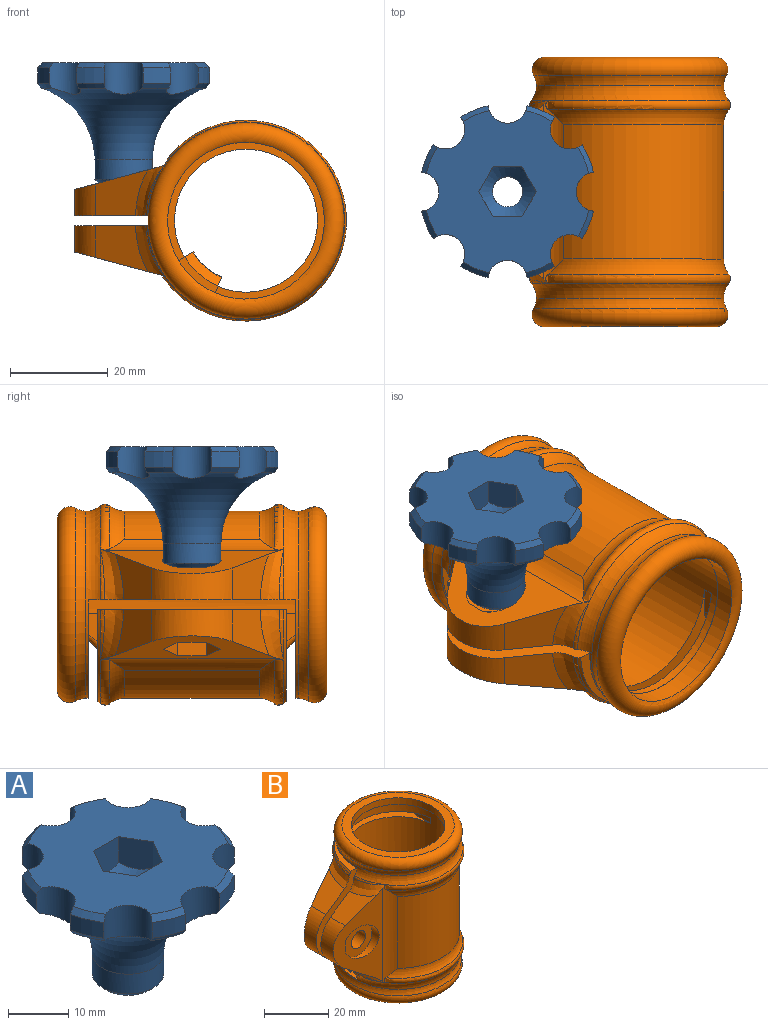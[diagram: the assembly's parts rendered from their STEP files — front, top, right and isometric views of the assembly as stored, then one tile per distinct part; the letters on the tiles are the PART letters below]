
ASSEMBLY  parts=2 mates=1
PART A: 45 faces, bbox 45.5x45.5x30.6 mm
  f0: plane 33.17x33.17mm, normal (0,0,1), area 688.8mm2, adj f2,f5,f8,f11,f14,f17,f21,f27
  f1: cone r=18mm half-angle=37.9deg, axis (0,0,1), area 7.3mm2, adj f23,f24,f36,f43
  f2: cone r=17mm half-angle=45deg, axis (0,0,-1), area 8.4mm2, adj f0,f24,f36,f43
  f3: cylinder r=18mm len=5.63mm, axis (0,0,1), area 19.6mm2, adj f4,f5,f42,f43
  f4: cone r=18mm half-angle=37.9deg, axis (0,0,1), area 7.3mm2, adj f3,f23,f42,f43
  f5: cone r=17mm half-angle=45deg, axis (0,0,-1), area 8.4mm2, adj f0,f3,f42,f43
  f6: cylinder r=18mm len=5.63mm, axis (0,0,1), area 19.6mm2, adj f7,f8,f41,f42
  f7: cone r=18mm half-angle=37.9deg, axis (0,0,1), area 7.3mm2, adj f6,f23,f41,f42
  f8: cone r=17mm half-angle=45deg, axis (0,0,-1), area 8.4mm2, adj f0,f6,f41,f42
  f9: cylinder r=18mm len=5.63mm, axis (0,0,1), area 19.6mm2, adj f10,f11,f40,f41
  f10: cone r=18mm half-angle=37.9deg, axis (0,0,1), area 7.3mm2, adj f9,f23,f40,f41
  f11: cone r=17mm half-angle=45deg, axis (0,0,-1), area 8.4mm2, adj f0,f9,f40,f41
  f12: cylinder r=18mm len=5.63mm, axis (0,0,1), area 19.6mm2, adj f13,f14,f39,f40
  f13: cone r=18mm half-angle=37.9deg, axis (0,0,1), area 7.3mm2, adj f12,f23,f39,f40
  f14: cone r=17mm half-angle=45deg, axis (0,0,-1), area 8.4mm2, adj f0,f12,f39,f40
  f15: cylinder r=18mm len=5.63mm, axis (0,0,1), area 19.6mm2, adj f16,f17,f38,f39
  f16: cone r=18mm half-angle=37.9deg, axis (0,0,1), area 7.3mm2, adj f15,f23,f38,f39
  f17: cone r=17mm half-angle=45deg, axis (0,0,-1), area 8.4mm2, adj f0,f15,f38,f39
  f18: cylinder r=18mm len=5.63mm, axis (0,0,1), area 19.6mm2, adj f20,f21,f37,f38
  f19: cylinder r=18mm len=5.63mm, axis (0,0,1), area 19.6mm2, adj f34,f35,f36,f37
  f20: cone r=18mm half-angle=37.9deg, axis (0,0,1), area 7.3mm2, adj f18,f23,f37,f38
  f21: cone r=17mm half-angle=45deg, axis (0,0,-1), area 8.4mm2, adj f0,f18,f37,f38
  f22: cylinder r=3.1mm len=16.72mm, axis (0,0,1), area 325.6mm2, adj f25,f44
  f23: torus R=20.9mm, axis (0,0,1), area 1085.1mm2, adj f1,f4,f7,f10,f13,f16,f20,f26
  f24: cylinder r=18mm len=5.63mm, axis (0,0,1), area 19.6mm2, adj f1,f2,f36,f43
  f25: plane 9.8x9.8mm, normal (0,0,-1), area 45.2mm2, adj f22,f33
  f26: cylinder r=5.9mm len=11.8mm, axis (0,0,1), area 148.3mm2, adj f23,f33
  f27: plane 6.01x5.1mm, normal (0.87,-0.5,0), area 33.7mm2, adj f0,f28,f32,f44
  f28: plane 6.01x5.1mm, normal (0.87,0.5,0), area 33.7mm2, adj f0,f27,f29,f44
  f29: plane 6.01x5.89mm, normal (0,1,0), area 33.7mm2, adj f0,f28,f30,f44
  f30: plane 6.29x5.38mm, normal (-0.87,0.5,0), area 33.7mm2, adj f0,f29,f31,f44
  f31: plane 6.01x5.1mm, normal (-0.87,-0.5,0), area 33.7mm2, adj f0,f30,f32,f44
  f32: plane 6.01x5.89mm, normal (0,-1,0), area 33.7mm2, adj f0,f27,f31,f44
  f33: cone r=5.9mm half-angle=45deg, axis (0,0,1), area 48mm2, adj f25,f26
  f34: cone r=18mm half-angle=37.9deg, axis (0,0,1), area 7.3mm2, adj f19,f23,f36,f37
  f35: cone r=17mm half-angle=45deg, axis (0,0,-1), area 8.4mm2, adj f0,f19,f36,f37
  f36: cylinder r=4mm len=7.95mm, axis (0,0,1), area 65.9mm2, adj f0,f1,f2,f19,f23,f24,f34,f35
  f37: cylinder r=4mm len=6.5mm, axis (0,0,1), area 65.9mm2, adj f0,f18,f19,f20,f21,f23,f34,f35
  f38: cylinder r=4mm len=7.95mm, axis (0,0,1), area 65.9mm2, adj f0,f15,f16,f17,f18,f20,f21,f23
  f39: cylinder r=4mm len=6.5mm, axis (0,0,1), area 65.9mm2, adj f0,f12,f13,f14,f15,f16,f17,f23
  f40: cylinder r=4mm len=7.95mm, axis (0,0,1), area 64.9mm2, adj f0,f9,f10,f11,f12,f13,f14,f23
  f41: cylinder r=4mm len=6.5mm, axis (0,0,1), area 65.9mm2, adj f0,f6,f7,f8,f9,f10,f11,f23
  f42: cylinder r=4mm len=7.95mm, axis (0,0,1), area 65.9mm2, adj f0,f3,f4,f5,f6,f7,f8,f23
  f43: cylinder r=4mm len=6.5mm, axis (0,0,1), area 65.9mm2, adj f0,f1,f2,f3,f4,f5,f23,f24
  f44: cone r=3.1mm half-angle=45deg, axis (0,0,1), area 84.9mm2, adj f22,f27,f28,f29,f30,f31,f32
PART B: 99 faces, bbox 63.5x50.8x61.3 mm
  f0: cylinder r=12.5mm len=5.83mm, axis (0,0,1), area 2.4mm2, adj f1,f96,f97,f98
  f1: cone r=12.5mm half-angle=45deg, axis (0,0,-1), area 6.9mm2, adj f0,f2,f96,f98
  f2: cone r=13.1mm half-angle=45deg, axis (0,0,1), area 5.7mm2, adj f1,f3,f96,f98
  f3: cone r=12.5mm half-angle=45deg, axis (0,0,-1), area 23mm2, adj f2,f4,f96,f98
  f4: plane 8.14x7.42mm, normal (0,0,-1), area 15.5mm2, adj f3,f5,f96,f98
  f5: cylinder r=16.1mm len=47.93mm, axis (0,0,-1), area 4368.8mm2, adj f4,f6,f58,f59,f60,f61,f62,f63
  f6: plane 38.5x18.97mm, normal (0,-1,0), area 431.9mm2, adj f5,f7,f38,f39,f40,f41,f42,f49
  f7: cylinder r=3.1mm len=6.51mm, axis (0,-1,0), area 126.8mm2, adj f6,f8
  f8: plane 11.78x10.2mm, normal (0,1,0), area 59.9mm2, adj f7,f9,f33,f34,f35,f36,f37
  f9: plane 5.1x2.94mm, normal (0.5,0,-0.87), area 5.1mm2, adj f8,f10,f33,f37
  f10: plane 37.81x19.56mm, normal (-0.26,0.97,0), area 303mm2, adj f9,f11,f33,f34,f35,f36,f37,f38
  f11: cylinder r=9mm len=36.95mm, axis (0,0,-1), area 151.5mm2, adj f10,f12,f27,f28,f29,f31,f40,f56
  f12: torus R=24.1mm, axis (0,0,-1), area 319.6mm2, adj f11,f13,f27,f31
  f13: cylinder r=9mm len=36.95mm, axis (0,0,-1), area 151.5mm2, adj f12,f14,f20,f24,f27,f28,f29,f31
  f14: bspline ~13.12x6.42mm, area 42.7mm2, adj f13,f15,f18,f19,f20,f42,f62
  f15: plane 10.75x9.41mm, normal (-0.58,0,0.82), area 84.9mm2, adj f14,f16,f20,f62
  f16: cylinder r=10mm len=16.34mm, axis (0,1,0), area 124.5mm2, adj f15,f17,f20,f62
  f17: plane 10.75x9.4mm, normal (-0.58,0,-0.82), area 84.9mm2, adj f16,f20,f24,f62
  f18: cylinder r=9mm len=0.26mm, axis (0,0,-1), area 0mm2, adj f14,f31,f42
  f19: torus R=19mm, axis (0,0,1), area 5mm2, adj f14,f42,f62
  f20: plane 41.85x23.6mm, normal (-0.26,-0.97,0), area 279.7mm2, adj f13,f14,f15,f16,f17,f21,f23,f24
  f21: plane 12x11.77mm, normal (0,-1,0), area 82.4mm2, adj f20,f22,f23
  f22: cylinder r=3.1mm len=6.51mm, axis (0,1,0), area 126.8mm2, adj f21,f62
  f23: cylinder r=6mm len=12mm, axis (0,-1,0), area 0mm2, adj f20,f21
  f24: bspline ~14.6x6.42mm, area 42.7mm2, adj f13,f17,f20,f25,f26,f49,f62
  f25: torus R=19mm, axis (0,0,1), area 5mm2, adj f24,f49,f62
  f26: cylinder r=9mm len=0.26mm, axis (0,0,-1), area 0mm2, adj f24,f29,f49
  f27: cylinder r=19.1mm len=38.2mm, axis (0,0,-1), area 2475.2mm2, adj f11,f12,f13,f28
  f28: torus R=24.1mm, axis (0,0,-1), area 319.6mm2, adj f11,f13,f27,f29
  f29: torus R=19mm, axis (0,0,1), area 209.4mm2, adj f11,f13,f26,f28,f30,f49
  f30: cylinder r=9mm len=0.26mm, axis (0,0,-1), area 0mm2, adj f29,f49,f56
  f31: torus R=19mm, axis (0,0,1), area 209.4mm2, adj f11,f12,f13,f18,f32,f42
  f32: cylinder r=9mm len=0.26mm, axis (0,0,-1), area 0mm2, adj f31,f40,f42
  f33: plane 5.89x0.18mm, normal (1,0,0), area 1mm2, adj f8,f9,f10,f34
  f34: plane 5.1x2.94mm, normal (0.5,0,0.87), area 5.1mm2, adj f8,f10,f33,f35
  f35: plane 5.1x2.94mm, normal (-0.5,0,0.87), area 13.1mm2, adj f8,f10,f34,f36
  f36: plane 5.89x2.91mm, normal (-1,0,0), area 17.1mm2, adj f8,f10,f35,f37
  f37: plane 5.1x2.94mm, normal (-0.5,0,-0.87), area 13.1mm2, adj f8,f9,f10,f36
  f38: cylinder r=10mm len=16.34mm, axis (0,-1,0), area 124.5mm2, adj f6,f10,f39,f57
  f39: plane 10.75x9.4mm, normal (-0.58,0,0.82), area 84.9mm2, adj f6,f10,f38,f40
  f40: bspline ~14.6x6.42mm, area 42.7mm2, adj f6,f10,f11,f32,f39,f41,f42
  f41: torus R=19mm, axis (0,0,1), area 5mm2, adj f6,f40,f42
  f42: torus R=24.1mm, axis (0,0,1), area 292.5mm2, adj f6,f14,f18,f19,f31,f32,f40,f41
  f43: torus R=24.09mm, axis (0,0,1), area 260.7mm2, adj f42,f44
  f44: torus R=17.5mm, axis (0,0,1), area 626.8mm2, adj f43,f45
  f45: plane 35x35mm, normal (0,0,1), area 292.5mm2, adj f44,f46
  f46: cylinder r=14.6mm len=29.2mm, axis (0,0,1), area 229.3mm2, adj f45,f63
  f47: bspline ~5.64x4.41mm, area 6.3mm2, adj f42,f48,f64,f66
  f48: plane 5.85x2mm, normal (-1,0,0), area 10mm2, adj f47,f64,f65,f66
  f49: torus R=24.1mm, axis (0,0,1), area 292.5mm2, adj f6,f24,f25,f26,f29,f30,f50,f52
  f50: bspline ~5.64x4.36mm, area 6.3mm2, adj f49,f51,f58,f61
  f51: plane 5.85x2mm, normal (-1,0,0), area 10mm2, adj f50,f58,f59,f61
  f52: torus R=24.09mm, axis (0,0,1), area 260.7mm2, adj f49,f53
  f53: torus R=17.5mm, axis (0,0,1), area 795.8mm2, adj f52,f54
  f54: cylinder r=16mm len=32mm, axis (0,0,1), area 402.1mm2, adj f53,f60
  f55: torus R=19mm, axis (0,0,1), area 5mm2, adj f6,f49,f56
  f56: bspline ~13.12x6.42mm, area 42.7mm2, adj f6,f10,f11,f30,f49,f55,f57
  f57: plane 10.75x9.41mm, normal (-0.58,0,-0.82), area 84.9mm2, adj f6,f10,f38,f56
  f58: plane 39.1x20.35mm, normal (0,0,-1), area 176.5mm2, adj f5,f6,f49,f50,f51,f59
  f59: cylinder r=1mm len=2mm, axis (0,0,-1), area 0.2mm2, adj f5,f51,f58,f61
  f60: torus R=17.5mm, axis (0,0,1), area 12.4mm2, adj f5,f54
  f61: plane 37.52x20.59mm, normal (0,0,1), area 151.6mm2, adj f5,f49,f50,f51,f59,f62
  f62: plane 42.51x18.97mm, normal (0,1,0), area 445mm2, adj f5,f14,f15,f16,f17,f19,f22,f24
  f63: plane 32.2x32.2mm, normal (0,0,-1), area 144.7mm2, adj f5,f46
  f64: plane 37.52x20.59mm, normal (0,0,-1), area 151.6mm2, adj f5,f42,f47,f48,f62,f65
  f65: cylinder r=1mm len=2mm, axis (0,0,-1), area 0.2mm2, adj f5,f48,f64,f66
  f66: plane 39.1x20.35mm, normal (0,0,1), area 191.9mm2, adj f5,f6,f42,f47,f48,f65,f67,f96
  f67: cone r=14.5mm half-angle=45deg, axis (0,0,1), area 24.1mm2, adj f66,f68,f96,f98
  f68: cone r=12.5mm half-angle=45deg, axis (0,0,-1), area 6.9mm2, adj f67,f69,f96,f98
  f69: cone r=13.1mm half-angle=45deg, axis (0,0,1), area 6.9mm2, adj f68,f70,f96,f98
  f70: cylinder r=12.5mm len=5.83mm, axis (0,0,1), area 2.4mm2, adj f69,f71,f96,f98
  f71: cone r=12.5mm half-angle=45deg, axis (0,0,-1), area 6.9mm2, adj f70,f72,f96,f98
  f72: cone r=13.1mm half-angle=45deg, axis (0,0,1), area 6.9mm2, adj f71,f73,f96,f98
  f73: cylinder r=12.5mm len=5.83mm, axis (0,0,1), area 2.4mm2, adj f72,f74,f96,f98
  f74: cone r=12.5mm half-angle=45deg, axis (0,0,-1), area 6.9mm2, adj f73,f75,f96,f98
  f75: cone r=13.1mm half-angle=45deg, axis (0,0,1), area 6.9mm2, adj f74,f76,f96,f98
  f76: cylinder r=12.5mm len=5.83mm, axis (0,0,1), area 2.4mm2, adj f75,f77,f96,f98
  f77: cone r=12.5mm half-angle=45deg, axis (0,0,-1), area 6.9mm2, adj f76,f78,f96,f98
  f78: cone r=13.1mm half-angle=45deg, axis (0,0,1), area 6.9mm2, adj f77,f79,f96,f98
  f79: cylinder r=12.5mm len=5.83mm, axis (0,0,1), area 2.4mm2, adj f78,f80,f96,f98
  f80: cone r=12.5mm half-angle=45deg, axis (0,0,-1), area 6.9mm2, adj f79,f81,f96,f98
  f81: cone r=13.1mm half-angle=45deg, axis (0,0,1), area 6.9mm2, adj f80,f82,f96,f98
  f82: cylinder r=12.5mm len=5.83mm, axis (0,0,1), area 2.4mm2, adj f81,f83,f96,f98
  f83: cone r=12.5mm half-angle=45deg, axis (0,0,-1), area 6.9mm2, adj f82,f84,f96,f98
  f84: cone r=13.1mm half-angle=45deg, axis (0,0,1), area 6.9mm2, adj f83,f85,f96,f98
  f85: cylinder r=12.5mm len=5.83mm, axis (0,0,1), area 2.4mm2, adj f84,f86,f96,f98
  f86: cone r=12.5mm half-angle=45deg, axis (0,0,-1), area 6.9mm2, adj f85,f87,f96,f98
  f87: cone r=13.1mm half-angle=45deg, axis (0,0,1), area 6.9mm2, adj f86,f88,f96,f98
  f88: cylinder r=12.5mm len=5.83mm, axis (0,0,1), area 2.4mm2, adj f87,f89,f96,f98
  f89: cone r=12.5mm half-angle=45deg, axis (0,0,-1), area 6.9mm2, adj f88,f90,f96,f98
  f90: cone r=13.1mm half-angle=45deg, axis (0,0,1), area 6.9mm2, adj f89,f91,f96,f98
  f91: cylinder r=12.5mm len=5.83mm, axis (0,0,1), area 2.4mm2, adj f90,f92,f96,f98
  f92: cone r=12.5mm half-angle=45deg, axis (0,0,-1), area 6.9mm2, adj f91,f93,f96,f98
  f93: cone r=13.1mm half-angle=45deg, axis (0,0,1), area 6.9mm2, adj f92,f94,f96,f98
  f94: cylinder r=12.5mm len=5.83mm, axis (0,0,1), area 2.4mm2, adj f93,f95,f96,f98
  f95: cone r=12.5mm half-angle=45deg, axis (0,0,-1), area 6.9mm2, adj f94,f96,f97,f98
  f96: plane 20x3.31mm, normal (0.92,0.39,0), area 64.1mm2, adj f0,f1,f2,f3,f4,f5,f66,f67
  f97: cone r=13.1mm half-angle=45deg, axis (0,0,1), area 6.9mm2, adj f0,f95,f96,f98
  f98: plane 20x3.1mm, normal (-0.51,-0.86,0), area 64mm2, adj f0,f1,f2,f3,f4,f5,f66,f67
PLACE A t=(-39.83,-41.45,3.14)mm
PLACE B rot(axis=(-1,0,0),90deg) t=(-14.83,-41.45,-4.36)mm
MATE revolute B.f7 <-> A.f1  axis (0,0,-1) through (-39.83,-41.45,3.14)mm
